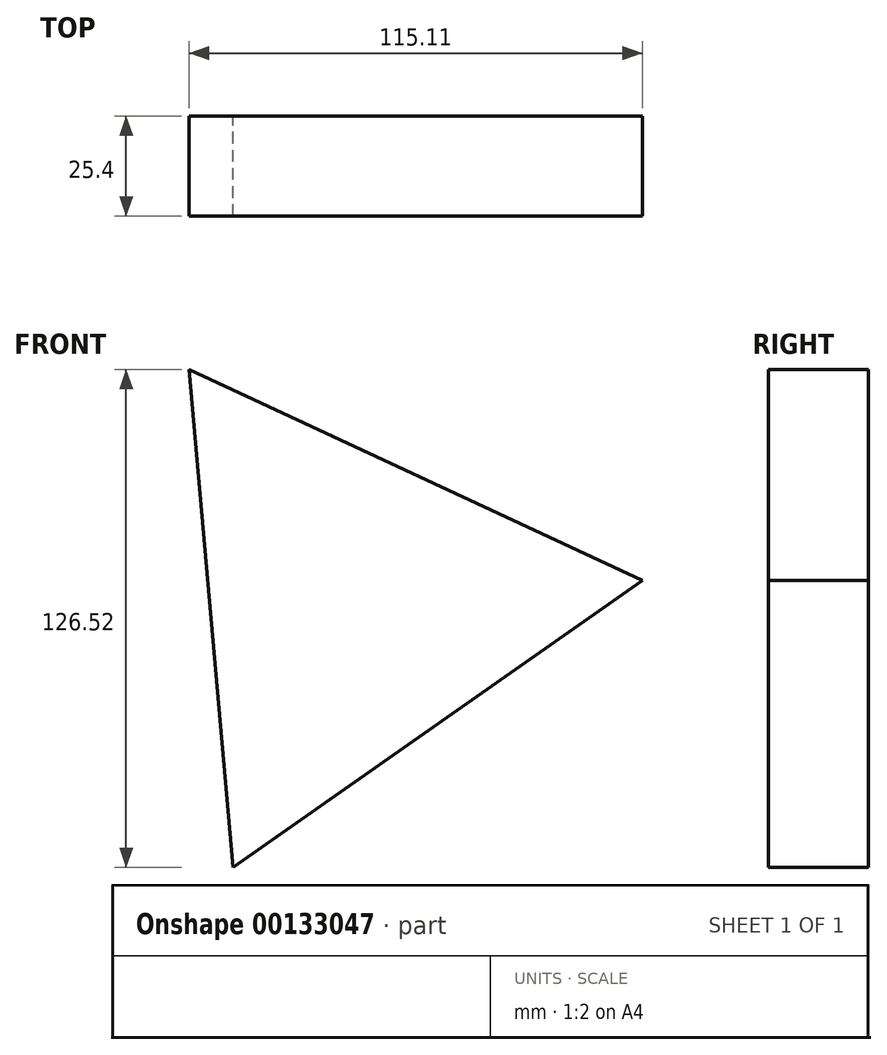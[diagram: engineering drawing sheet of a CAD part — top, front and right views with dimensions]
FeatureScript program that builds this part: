
annotation { "Feature Type Name" : "Feature", "Feature Type Description" : "" }
export const myFeature = defineFeature(function(context is Context, id is Id, definition is map)
    precondition{}
    {
        {
            var Q0;
            Q0=qCreatedBy(makeId("Front.planeOp"),FACE);
            var sketch = newSketch(context, id + "F0", { "sketchPlane" : qUnion([Q0])});
            skCircle(sketch, "E0.cCircle", {"center": v(0, 0) * mm, "radius": 73.32 * mm, "construction": true});
            skLineSegment(sketch, "E0.0", {"start": v(-42.07, 60.06) * mm, "end": v(73.04, 6.4) * mm});
            skLineSegment(sketch, "E0.1", {"start": v(73.04, 6.4) * mm, "end": v(-30.98, -66.46) * mm});
            skLineSegment(sketch, "E0.2", {"start": v(-30.98, -66.46) * mm, "end": v(-42.07, 60.06) * mm});
            skSolve(sketch);
        }
        {
            var Q0;
            Q0 = qSketchRegion(id + "F0", true);
            var Q1;
            Q1=makeQuery(id+"F0.imprint","IMPRINT",FACE,{"disambiguationData":[TD([[makeQuery(id+"F0.imprint","IMPRINT",EDGE,{"derivedFrom":sQuery(id+"F0.wireOp",EDGE,"E0.0")}),-1.0]])]});
            extrude(context, id + "F1", {"entities" : qUnion([Q0, Q1]), "depth" : 25.4 * mm});
        }
    });
